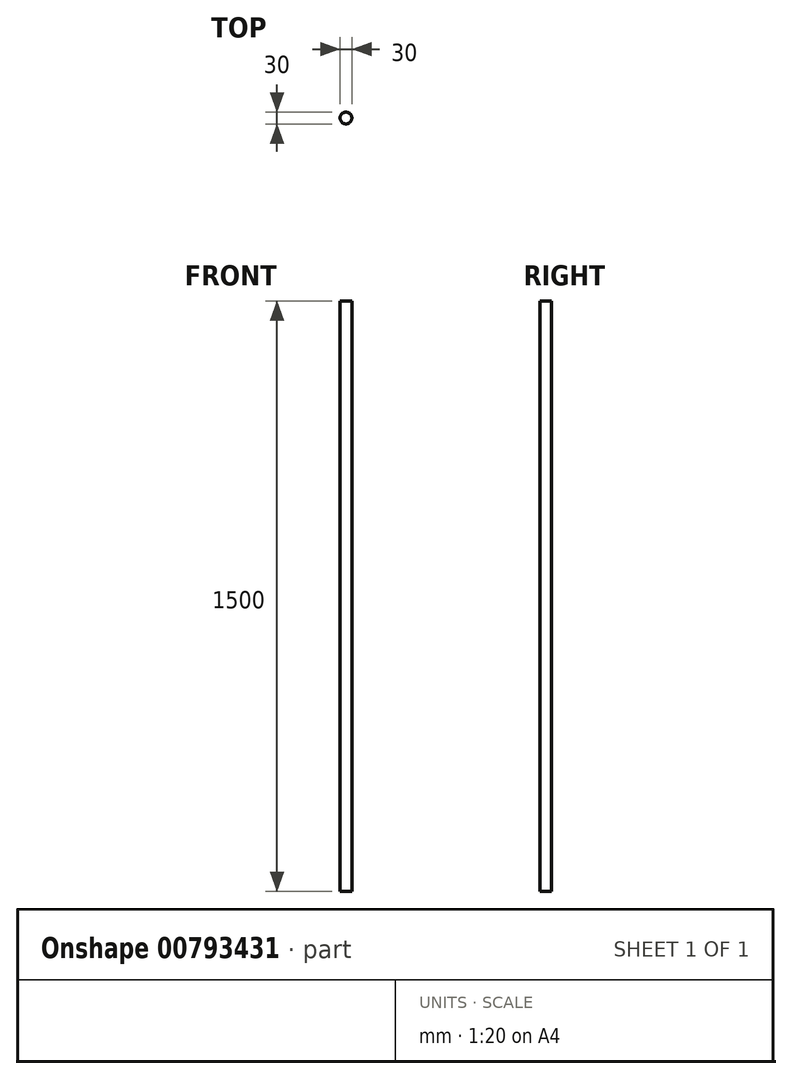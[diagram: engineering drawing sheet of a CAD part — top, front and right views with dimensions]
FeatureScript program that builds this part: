
annotation { "Feature Type Name" : "Feature", "Feature Type Description" : "" }
export const myFeature = defineFeature(function(context is Context, id is Id, definition is map)
    precondition{}
    {
        {
            var Q0;
            Q0=qCreatedBy(makeId("Right.planeOp"),FACE);
            var sketch = newSketch(context, id + "F0", { "sketchPlane" : qUnion([Q0])});
            skLineSegment(sketch, "E0", {"start": v(0, 0) * mm, "end": v(0, 1500) * mm});
            skSolve(sketch);
        }
        {
            var Q0;
            Q0=qCreatedBy(makeId("Top.planeOp"),FACE);
            var sketch = newSketch(context, id + "F1", { "sketchPlane" : qUnion([Q0])});
            skCircle(sketch, "E1", {"center": v(0, 0) * mm, "radius": 15 * mm});
            skSolve(sketch);
        }
        {
            var Q0;
            Q0=makeQuery(id+"F1.imprint","IMPRINT",FACE,{"disambiguationData":[TD([[makeQuery(id+"F1.imprint","IMPRINT",EDGE,{"derivedFrom":sQuery(id+"F1.wireOp",EDGE,"E1")}),1.0]])]});
            var Q1;
            Q1=sQuery(id+"F0.wireOp",EDGE,"E0");
            sweep(context, id + "F2", {"profiles" : qUnion([Q0]), "path" : qUnion([Q1])});
        }
    });
